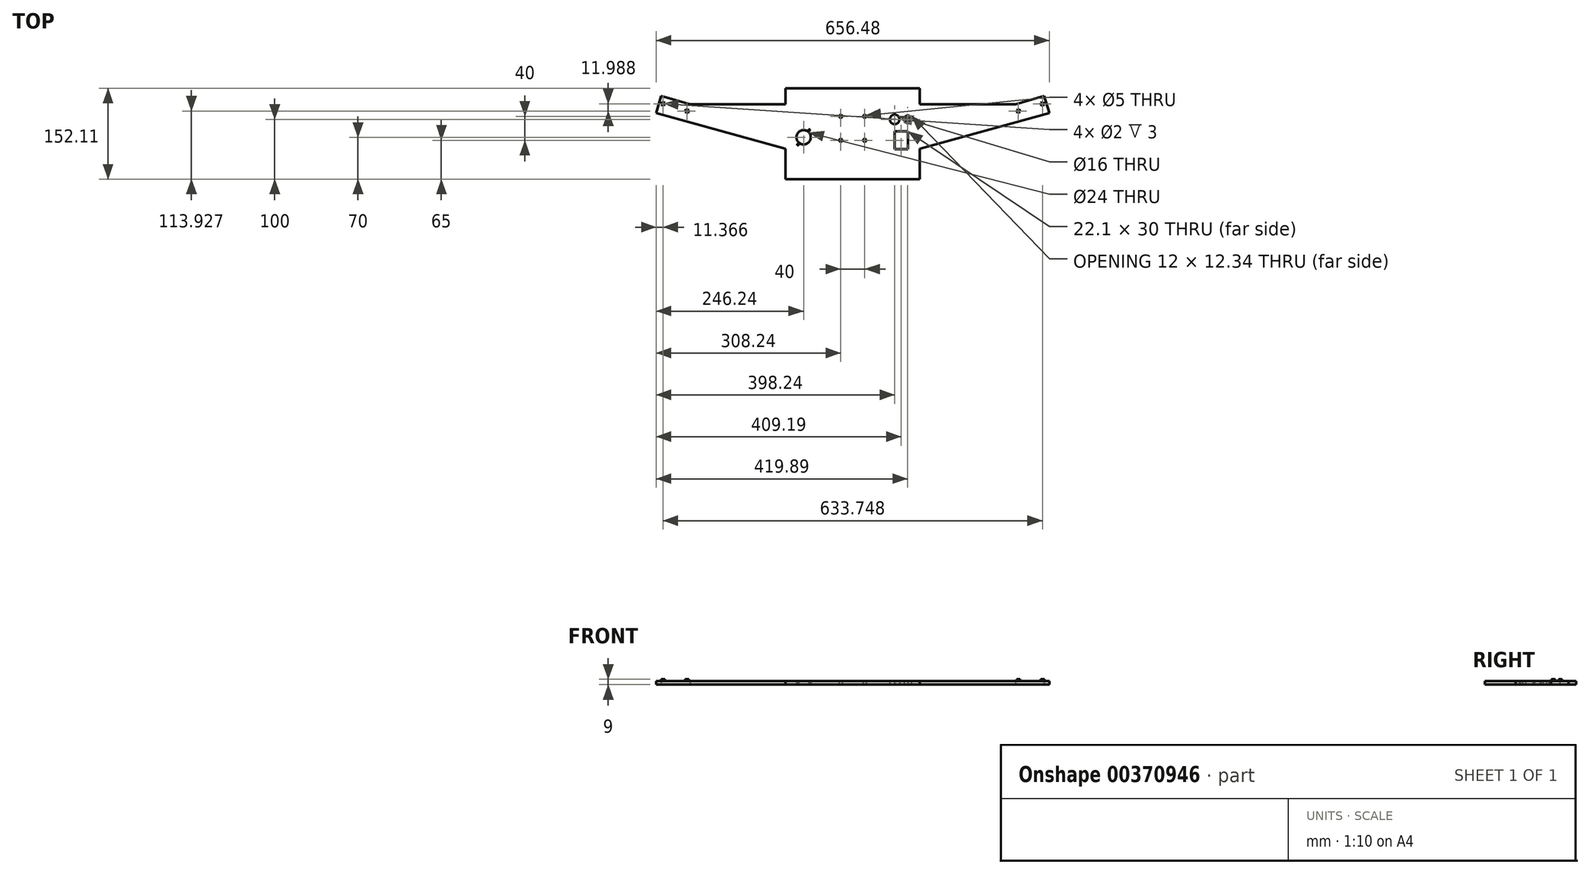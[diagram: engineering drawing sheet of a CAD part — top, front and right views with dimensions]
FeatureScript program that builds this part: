
annotation { "Feature Type Name" : "Feature", "Feature Type Description" : "" }
export const myFeature = defineFeature(function(context is Context, id is Id, definition is map)
    precondition{}
    {
        {
            var Q0;
            Q0=qCreatedBy(makeId("Top.planeOp"),FACE);
            var sketch = newSketch(context, id + "F0", { "sketchPlane" : qUnion([Q0])});
            skLineSegment(sketch, "E0.top", {"start": v(0, -125) * mm, "end": v(224, -125) * mm});
            skLineSegment(sketch, "E0.left", {"start": v(0, -73.9) * mm, "end": v(0, -125) * mm});
            skLineSegment(sketch, "E0.right", {"start": v(224, -73.9) * mm, "end": v(224, -125) * mm});
            skLineSegment(sketch, "E1", {"start": v(224, 0) * mm, "end": v(383.76, 0) * mm});
            skLineSegment(sketch, "E2", {"start": v(383.76, 0) * mm, "end": v(431.68, 14.27) * mm});
            skLineSegment(sketch, "E3", {"start": v(431.68, 14.27) * mm, "end": v(440.24, -14.48) * mm});
            skLineSegment(sketch, "E4", {"start": v(440.24, -14.48) * mm, "end": v(383.76, -30) * mm});
            skLineSegment(sketch, "E5", {"start": v(383.76, -30) * mm, "end": v(224, -73.9) * mm});
            skLineSegment(sketch, "E6", {"start": v(0, 0) * mm, "end": v(-159.76, 0) * mm});
            skLineSegment(sketch, "E7", {"start": v(-159.76, 0) * mm, "end": v(-207.68, 14.27) * mm});
            skLineSegment(sketch, "E8", {"start": v(-207.68, 14.27) * mm, "end": v(-216.24, -14.48) * mm});
            skLineSegment(sketch, "E9", {"start": v(-216.24, -14.48) * mm, "end": v(-159.76, -30) * mm});
            skLineSegment(sketch, "E10", {"start": v(-159.76, -30) * mm, "end": v(0, -73.9) * mm});
            skPoint(sketch, "E11", {"position": v(-188, -7.24) * mm});
            skPoint(sketch, "E12", {"position": v(412, -7.24) * mm});
            skLineSegment(sketch, "E13.top", {"start": v(224, 27.11) * mm, "end": v(0, 27.11) * mm});
            skLineSegment(sketch, "E13.left", {"start": v(224, 0) * mm, "end": v(224, 27.11) * mm});
            skLineSegment(sketch, "E13.right", {"start": v(0, -2.89) * mm, "end": v(0, 27.11) * mm});
            skSolve(sketch);
        }
        {
            var Q0;
            Q0=makeQuery(id+"F0.imprint","IMPRINT",FACE,{"disambiguationData":[TD([[makeQuery(id+"F0.imprint","IMPRINT",EDGE,{"derivedFrom":sQuery(id+"F0.wireOp",EDGE,"E0.top")}),1.0]])]});
            extrude(context, id + "F1", {"entities" : qUnion([Q0]), "depth" : 6 * mm});
        }
        {
            var Q0;
            Q0=makeQuery(id+"F1.opExtrude","CAP_FACE",FACE,{"disambiguationData":[OSD([sQuery(id+"F0.wireOp",EDGE,"E0.bottom"),sQuery(id+"F0.wireOp",EDGE,"E0.top"),sQuery(id+"F0.wireOp",EDGE,"E0.left"),sQuery(id+"F0.wireOp",EDGE,"E0.right"),sQuery(id+"F0.wireOp",EDGE,"E1"),sQuery(id+"F0.wireOp",EDGE,"E2"),sQuery(id+"F0.wireOp",EDGE,"E3"),sQuery(id+"F0.wireOp",EDGE,"E4"),sQuery(id+"F0.wireOp",EDGE,"E5"),sQuery(id+"F0.wireOp",EDGE,"E6"),sQuery(id+"F0.wireOp",EDGE,"E7"),sQuery(id+"F0.wireOp",EDGE,"E8"),sQuery(id+"F0.wireOp",EDGE,"E9"),sQuery(id+"F0.wireOp",EDGE,"E10"),sQuery(id+"F0.wireOp",EDGE,"gANkgMz7-IP7v-wW6s-PRGa-iH9qDQyWt3tI"),sQuery(id+"F0.wireOp",EDGE,"Pi1Q3kOB-2sir-CNe2-Qde5-uYZxFTxFElgx")])],"isStart":true});
            var sketch = newSketch(context, id + "F2", { "sketchPlane" : qUnion([Q0])});
            skLineSegment(sketch, "E14", {"start": v(441.72, 107.02) * mm, "end": v(112, -1000.05) * mm});
            skLineSegment(sketch, "E15", {"start": v(-221.85, 120.9) * mm, "end": v(112, -1000.05) * mm});
            skLineSegment(sketch, "E16", {"start": v(112, -1000.05) * mm, "end": v(95.74, 18.11) * mm});
            skSolve(sketch);
        }
        {
            var Q0;
            Q0=makeQuery(id+"F2.imprint","IMPRINT",FACE,{"disambiguationData":[TD([[makeQuery(id+"F2.imprint","IMPRINT",EDGE,{"derivedFrom":makeQuery(id+"F1.opExtrude","CAP_EDGE",EDGE,{"disambiguationData":[OSD([sQuery(id+"F0.wireOp",EDGE,"E0.top")])],"isStart":true})}),-1.0]])]});
            var sketch = newSketch(context, id + "F3", { "sketchPlane" : qUnion([Q0])});
            skCircle(sketch, "E17", {"center": v(132, 60) * mm, "radius": 2.5 * mm});
            skCircle(sketch, "E18.0.1.0", {"center": v(132, 20) * mm, "radius": 2.5 * mm});
            skCircle(sketch, "E18.1.0.0", {"center": v(92, 60) * mm, "radius": 2.5 * mm});
            skCircle(sketch, "E18.1.1.0", {"center": v(92, 20) * mm, "radius": 2.5 * mm});
            skLineSegment(sketch, "E18.direction1", {"start": v(132, 60) * mm, "end": v(92, 60) * mm, "construction": true});
            skLineSegment(sketch, "E18.direction2", {"start": v(132, 60) * mm, "end": v(132, 20) * mm, "construction": true});
            skSolve(sketch);
        }
        {
            var Q0;
            Q0 = qSketchRegion(id + "F3", true);
            extrude(context, id + "F4", {"entities" : qUnion([Q0]), "operationType" : NewBodyOperationType.REMOVE, "oppositeDirection" : true, "depth" : 25 * mm});
        }
        {
            var Q0;
            Q0=makeQuery(id+"F2.imprint","IMPRINT",FACE,{"disambiguationData":[TD([[makeQuery(id+"F2.imprint","IMPRINT",EDGE,{"derivedFrom":makeQuery(id+"F1.opExtrude","CAP_EDGE",EDGE,{"disambiguationData":[OSD([sQuery(id+"F0.wireOp",EDGE,"E0.top")])],"isStart":true})}),-1.0]])]});
            var sketch = newSketch(context, id + "F5", { "sketchPlane" : qUnion([Q0])});
            skLineSegment(sketch, "E19.bottom", {"start": v(181.9, 75) * mm, "end": v(204, 75) * mm});
            skLineSegment(sketch, "E19.top", {"start": v(181.9, 45) * mm, "end": v(204, 45) * mm});
            skLineSegment(sketch, "E19.left", {"start": v(181.9, 75) * mm, "end": v(181.9, 45) * mm});
            skLineSegment(sketch, "E19.right", {"start": v(204, 75) * mm, "end": v(204, 45) * mm});
            skSolve(sketch);
        }
        {
            var Q0;
            Q0 = qSketchRegion(id + "F5", true);
            extrude(context, id + "F6", {"entities" : qUnion([Q0]), "operationType" : NewBodyOperationType.REMOVE, "oppositeDirection" : true, "depth" : 25 * mm});
        }
        {
            var Q0;
            Q0=makeQuery(id+"F2.imprint","IMPRINT",FACE,{"disambiguationData":[TD([[makeQuery(id+"F2.imprint","IMPRINT",EDGE,{"derivedFrom":makeQuery(id+"F1.opExtrude","CAP_EDGE",EDGE,{"disambiguationData":[OSD([sQuery(id+"F0.wireOp",EDGE,"E0.top")])],"isStart":true})}),-1.0]])]});
            var sketch = newSketch(context, id + "F7", { "sketchPlane" : qUnion([Q0])});
            skLineSegment(sketch, "E20", {"start": v(209.65, 27.9) * mm, "end": v(209.65, 22.1) * mm});
            skArc(sketch, "E21", {"start": v(209.65, 27.9) * mm, "mid": v(197.65, 25) * mm, "end": v(209.65, 22.1) * mm});
            skCircle(sketch, "E22", {"center": v(182, 25) * mm, "radius": 8 * mm});
            skCircle(sketch, "E23", {"center": v(30, 55) * mm, "radius": 12 * mm});
            skCircle(sketch, "E24", {"center": v(20.5, 67) * mm, "radius": 1.25 * mm});
            skCircle(sketch, "E25", {"center": v(39.5, 43) * mm, "radius": 1.25 * mm});
            skSolve(sketch);
        }
        {
            var Q0;
            Q0 = qSketchRegion(id + "F7", true);
            extrude(context, id + "F8", {"entities" : qUnion([Q0]), "operationType" : NewBodyOperationType.REMOVE, "oppositeDirection" : true, "depth" : 25 * mm});
        }
        {
            var Q0;
            Q0=makeQuery(id+"F1.opExtrude","CAP_FACE",FACE,{"disambiguationData":[OSD([sQuery(id+"F0.wireOp",EDGE,"E0.top"),sQuery(id+"F0.wireOp",EDGE,"E0.left"),sQuery(id+"F0.wireOp",EDGE,"E0.right"),sQuery(id+"F0.wireOp",EDGE,"E1"),sQuery(id+"F0.wireOp",EDGE,"E2"),sQuery(id+"F0.wireOp",EDGE,"E3"),sQuery(id+"F0.wireOp",EDGE,"E4"),sQuery(id+"F0.wireOp",EDGE,"E5"),sQuery(id+"F0.wireOp",EDGE,"E6"),sQuery(id+"F0.wireOp",EDGE,"E7"),sQuery(id+"F0.wireOp",EDGE,"E8"),sQuery(id+"F0.wireOp",EDGE,"E9"),sQuery(id+"F0.wireOp",EDGE,"E10"),sQuery(id+"F0.wireOp",EDGE,"gANkgMz7-IP7v-wW6s-PRGa-iH9qDQyWt3tI"),sQuery(id+"F0.wireOp",EDGE,"Pi1Q3kOB-2sir-CNe2-Qde5-uYZxFTxFElgx"),sQuery(id+"F0.wireOp",EDGE,"x39UCTBA-Dsmu-YyPk-BvOc-zUcPAPyc9Iz9"),sQuery(id+"F0.wireOp",EDGE,"7bJB2XQq-EKbz-zbY9-MSUr-7B5ZE8ZpNaCk"),sQuery(id+"F0.wireOp",EDGE,"E13.top"),sQuery(id+"F0.wireOp",EDGE,"E13.left"),sQuery(id+"F0.wireOp",EDGE,"E13.right")])],"isStart":false});
            var sketch = newSketch(context, id + "F9", { "sketchPlane" : qUnion([Q0])});
            skLineSegment(sketch, "E26.bottom", {"start": v(425.76, 2.6) * mm, "end": v(430.56, 4.03) * mm});
            skLineSegment(sketch, "E26.top", {"start": v(427.2, -2.2) * mm, "end": v(431.98, -0.77) * mm});
            skLineSegment(sketch, "E26.left", {"start": v(425.76, 2.6) * mm, "end": v(427.2, -2.2) * mm});
            skLineSegment(sketch, "E26.right", {"start": v(430.56, 4.03) * mm, "end": v(431.98, -0.77) * mm});
            skCircle(sketch, "E27", {"center": v(428.87, 0.92) * mm, "radius": 1 * mm});
            skLineSegment(sketch, "E28.1.0.0", {"start": v(385.51, -9.4) * mm, "end": v(390.3, -7.96) * mm});
            skLineSegment(sketch, "E28.1.0.1", {"start": v(385.51, -9.4) * mm, "end": v(386.94, -14.18) * mm});
            skLineSegment(sketch, "E28.1.0.2", {"start": v(386.94, -14.18) * mm, "end": v(391.73, -12.76) * mm});
            skLineSegment(sketch, "E28.1.0.3", {"start": v(390.3, -7.96) * mm, "end": v(391.73, -12.76) * mm});
            skCircle(sketch, "E28.1.0.4", {"center": v(388.62, -11.07) * mm, "radius": 1 * mm});
            skLineSegment(sketch, "E28.direction1", {"start": v(425.76, 2.6) * mm, "end": v(385.51, -9.4) * mm, "construction": true});
            skSolve(sketch);
        }
        {
            var Q0;
            Q0 = qSketchRegion(id + "F9", true);
            extrude(context, id + "F10", {"entities" : qUnion([Q0]), "operationType" : NewBodyOperationType.ADD, "depth" : 3 * mm});
        }
        {
            var Q0;
            Q0=makeQuery(id+"F1.opExtrude","CAP_FACE",FACE,{"disambiguationData":[OSD([sQuery(id+"F0.wireOp",EDGE,"E0.top"),sQuery(id+"F0.wireOp",EDGE,"E0.left"),sQuery(id+"F0.wireOp",EDGE,"E0.right"),sQuery(id+"F0.wireOp",EDGE,"E1"),sQuery(id+"F0.wireOp",EDGE,"E2"),sQuery(id+"F0.wireOp",EDGE,"E3"),sQuery(id+"F0.wireOp",EDGE,"E4"),sQuery(id+"F0.wireOp",EDGE,"E5"),sQuery(id+"F0.wireOp",EDGE,"E6"),sQuery(id+"F0.wireOp",EDGE,"E7"),sQuery(id+"F0.wireOp",EDGE,"E8"),sQuery(id+"F0.wireOp",EDGE,"E9"),sQuery(id+"F0.wireOp",EDGE,"E10"),sQuery(id+"F0.wireOp",EDGE,"gANkgMz7-IP7v-wW6s-PRGa-iH9qDQyWt3tI"),sQuery(id+"F0.wireOp",EDGE,"Pi1Q3kOB-2sir-CNe2-Qde5-uYZxFTxFElgx"),sQuery(id+"F0.wireOp",EDGE,"x39UCTBA-Dsmu-YyPk-BvOc-zUcPAPyc9Iz9"),sQuery(id+"F0.wireOp",EDGE,"7bJB2XQq-EKbz-zbY9-MSUr-7B5ZE8ZpNaCk"),sQuery(id+"F0.wireOp",EDGE,"E13.top"),sQuery(id+"F0.wireOp",EDGE,"E13.left"),sQuery(id+"F0.wireOp",EDGE,"E13.right")])],"isStart":false});
            var sketch = newSketch(context, id + "F11", { "sketchPlane" : qUnion([Q0])});
            skLineSegment(sketch, "E29.bottom", {"start": v(-201.76, 2.6) * mm, "end": v(-206.56, 4.03) * mm});
            skLineSegment(sketch, "E29.top", {"start": v(-203.2, -2.2) * mm, "end": v(-207.98, -0.77) * mm});
            skLineSegment(sketch, "E29.left", {"start": v(-201.76, 2.6) * mm, "end": v(-203.2, -2.2) * mm});
            skLineSegment(sketch, "E29.right", {"start": v(-206.56, 4.03) * mm, "end": v(-207.98, -0.77) * mm});
            skCircle(sketch, "E30", {"center": v(-204.87, 0.92) * mm, "radius": 1 * mm});
            skLineSegment(sketch, "E31.1.0.0", {"start": v(-161.51, -9.4) * mm, "end": v(-166.3, -7.96) * mm});
            skLineSegment(sketch, "E31.1.0.1", {"start": v(-166.3, -7.96) * mm, "end": v(-167.73, -12.76) * mm});
            skLineSegment(sketch, "E31.1.0.2", {"start": v(-162.94, -14.18) * mm, "end": v(-167.73, -12.76) * mm});
            skLineSegment(sketch, "E31.1.0.3", {"start": v(-161.51, -9.4) * mm, "end": v(-162.94, -14.18) * mm});
            skCircle(sketch, "E31.1.0.4", {"center": v(-164.62, -11.07) * mm, "radius": 1 * mm});
            skLineSegment(sketch, "E31.direction1", {"start": v(-206.56, 4.03) * mm, "end": v(-166.3, -7.96) * mm, "construction": true});
            skSolve(sketch);
        }
        {
            var Q0;
            Q0 = qSketchRegion(id + "F11", true);
            extrude(context, id + "F12", {"entities" : qUnion([Q0]), "operationType" : NewBodyOperationType.ADD, "depth" : 3 * mm});
        }
    });
